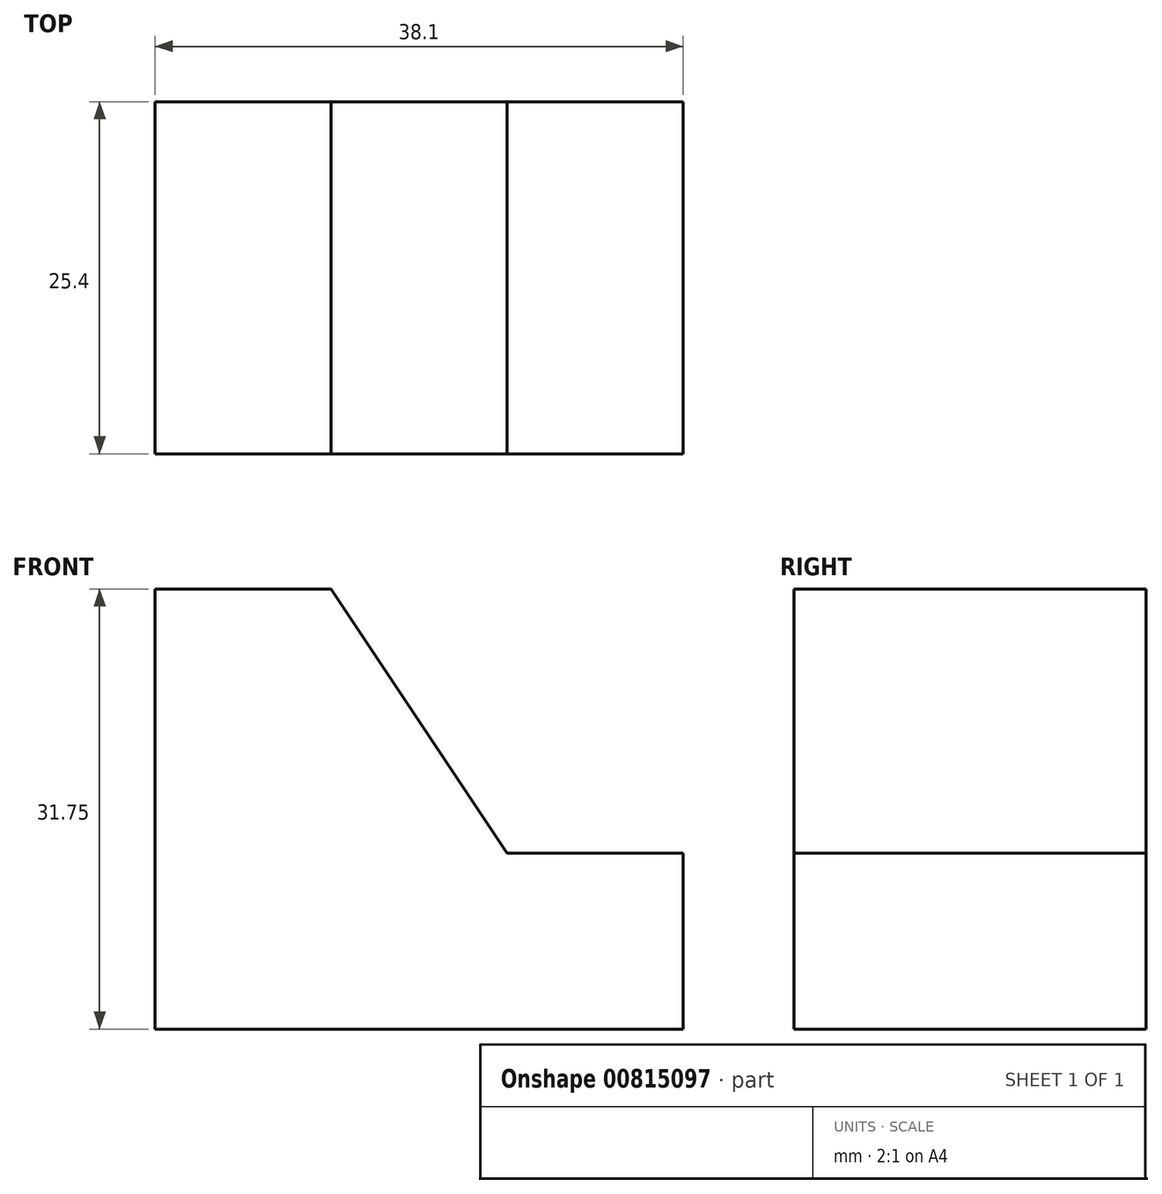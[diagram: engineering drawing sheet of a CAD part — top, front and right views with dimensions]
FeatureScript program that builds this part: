
annotation { "Feature Type Name" : "Feature", "Feature Type Description" : "" }
export const myFeature = defineFeature(function(context is Context, id is Id, definition is map)
    precondition{}
    {
        {
            var Q0;
            Q0=qCreatedBy(makeId("Front.planeOp"),FACE);
            var sketch = newSketch(context, id + "F0", { "sketchPlane" : qUnion([Q0])});
            skLineSegment(sketch, "E0", {"start": v(0, 0) * mm, "end": v(38.1, 0) * mm});
            skLineSegment(sketch, "E1", {"start": v(38.1, 0) * mm, "end": v(38.1, 12.7) * mm});
            skLineSegment(sketch, "E2", {"start": v(0, 0) * mm, "end": v(0, 31.75) * mm});
            skLineSegment(sketch, "E3", {"start": v(0, 31.75) * mm, "end": v(12.7, 31.75) * mm});
            skLineSegment(sketch, "E4", {"start": v(38.1, 12.7) * mm, "end": v(25.4, 12.7) * mm});
            skLineSegment(sketch, "E5", {"start": v(12.7, 31.75) * mm, "end": v(25.4, 12.7) * mm});
            skSolve(sketch);
        }
        {
            var Q0;
            Q0=makeQuery(id+"F0.imprint","IMPRINT",FACE,{"disambiguationData":[TD([[makeQuery(id+"F0.imprint","IMPRINT",EDGE,{"derivedFrom":sQuery(id+"F0.wireOp",EDGE,"E0")}),1.0]])]});
            extrude(context, id + "F1", {"entities" : qUnion([Q0]), "depth" : 25.4 * mm, "offsetDistance" : 25.4 * mm});
        }
    });
